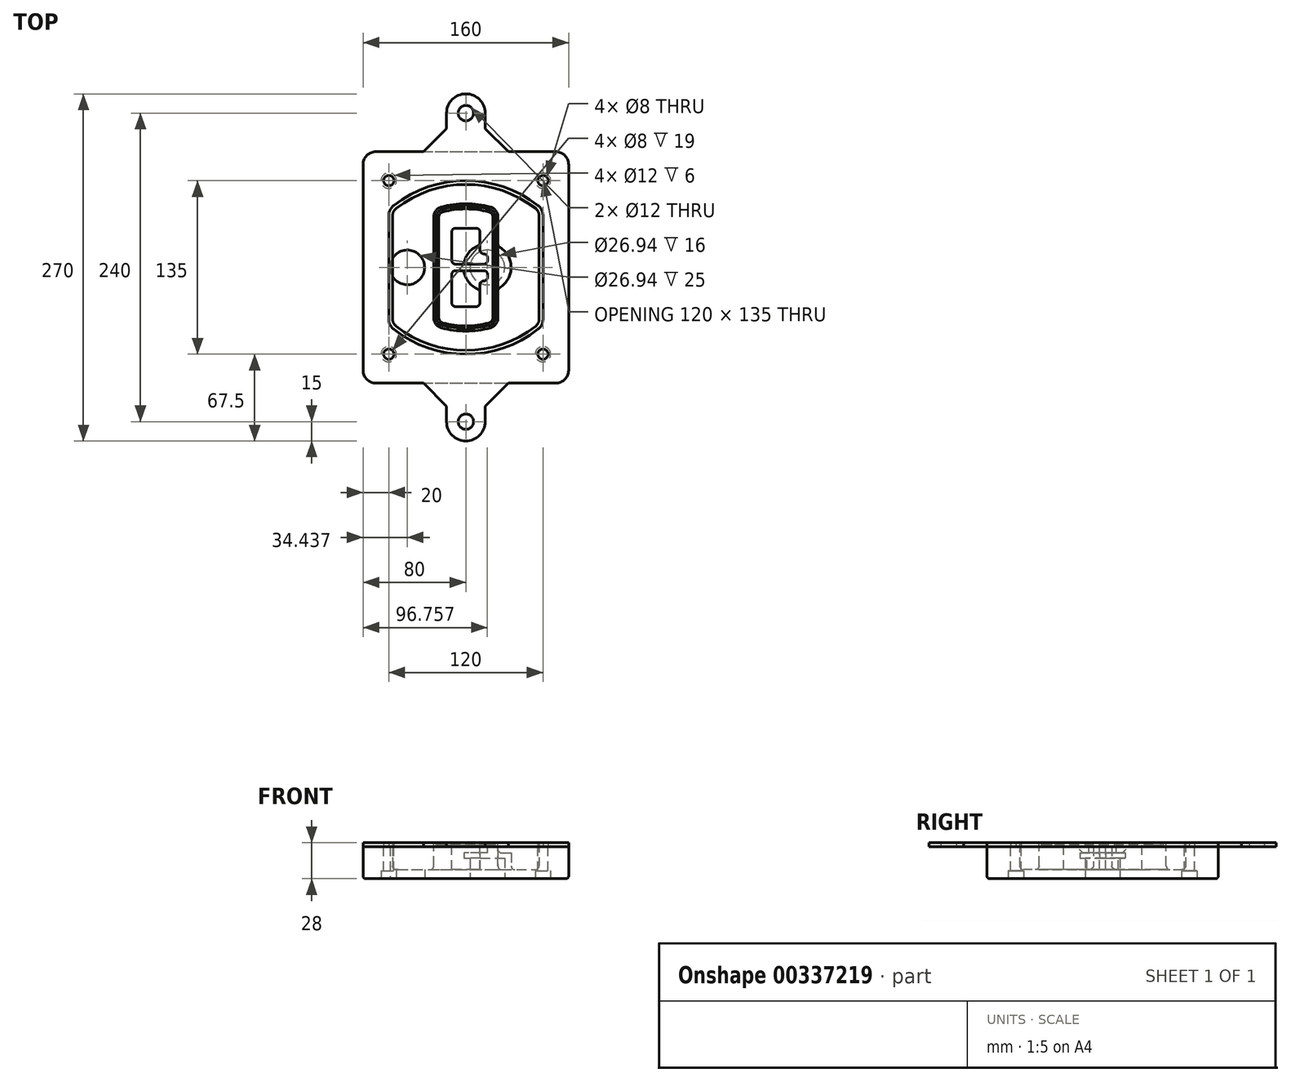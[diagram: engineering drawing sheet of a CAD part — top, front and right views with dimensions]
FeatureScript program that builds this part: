
annotation { "Feature Type Name" : "Feature", "Feature Type Description" : "" }
export const myFeature = defineFeature(function(context is Context, id is Id, definition is map)
    precondition{}
    {
        {
            var Q0;
            Q0=qCreatedBy(makeId("Top.planeOp"),FACE);
            var sketch = newSketch(context, id + "F0", { "sketchPlane" : qUnion([Q0])});
            skPoint(sketch, "E0.rect.middle", {"position": v(0, 0) * mm});
            skLineSegment(sketch, "E1.bottom", {"start": v(-70, -90) * mm, "end": v(70, -90) * mm});
            skLineSegment(sketch, "E1.top", {"start": v(-70, 90) * mm, "end": v(70, 90) * mm});
            skLineSegment(sketch, "E1.left", {"start": v(-80, -80) * mm, "end": v(-80, 80) * mm});
            skLineSegment(sketch, "E1.right", {"start": v(80, -80) * mm, "end": v(80, 80) * mm});
            skLineSegment(sketch, "E2", {"start": v(-80, 90) * mm, "end": v(80, -90) * mm, "construction": true});
            skLineSegment(sketch, "E3", {"start": v(80, 90) * mm, "end": v(-80, -90) * mm, "construction": true});
            skCircle(sketch, "E4", {"center": v(-60, 67.5) * mm, "radius": 4 * mm});
            skCircle(sketch, "E5", {"center": v(60, 67.5) * mm, "radius": 4 * mm});
            skCircle(sketch, "E6", {"center": v(60, -67.5) * mm, "radius": 4 * mm});
            skCircle(sketch, "E7", {"center": v(-60, -67.5) * mm, "radius": 4 * mm});
            skLineSegment(sketch, "E8", {"start": v(-60, 67.5) * mm, "end": v(60, 67.5) * mm, "construction": true});
            skLineSegment(sketch, "E9", {"start": v(60, 67.5) * mm, "end": v(60, -67.5) * mm, "construction": true});
            skLineSegment(sketch, "E10", {"start": v(60, -67.5) * mm, "end": v(-60, -67.5) * mm, "construction": true});
            skLineSegment(sketch, "E11", {"start": v(-60, -67.5) * mm, "end": v(-60, 67.5) * mm, "construction": true});
            skLineSegment(sketch, "E12", {"start": v(-60, 40.3) * mm, "end": v(-60, -40.3) * mm});
            skLineSegment(sketch, "E13", {"start": v(60, 40.3) * mm, "end": v(60, -40.3) * mm});
            skArc(sketch, "E14", {"start": v(56.15, 48.18) * mm, "mid": v(0, 67.5) * mm, "end": v(-56.15, 48.18) * mm});
            skArc(sketch, "E15", {"start": v(-56.15, -48.18) * mm, "mid": v(0, -67.5) * mm, "end": v(56.15, -48.18) * mm});
            skLineSegment(sketch, "E16", {"start": v(-60, 0) * mm, "end": v(60, 0) * mm, "construction": true});
            skPoint(sketch, "E17.visualSharp", {"position": v(-60, -45) * mm});
            skArc(sketch, "E17.filletArc", {"start": v(-60, -40.3) * mm, "mid": v(-58.99, -44.68) * mm, "end": v(-56.15, -48.18) * mm});
            skPoint(sketch, "E18.visualSharp", {"position": v(-60, 45) * mm});
            skArc(sketch, "E18.filletArc", {"start": v(-56.15, 48.18) * mm, "mid": v(-58.99, 44.68) * mm, "end": v(-60, 40.3) * mm});
            skPoint(sketch, "E19.visualSharp", {"position": v(60, 45) * mm});
            skArc(sketch, "E19.filletArc", {"start": v(60, 40.3) * mm, "mid": v(58.99, 44.68) * mm, "end": v(56.15, 48.18) * mm});
            skPoint(sketch, "E20.visualSharp", {"position": v(60, -45) * mm});
            skArc(sketch, "E20.filletArc", {"start": v(56.15, -48.18) * mm, "mid": v(58.99, -44.68) * mm, "end": v(60, -40.3) * mm});
            skPoint(sketch, "E21.visualSharp", {"position": v(-80, 90) * mm});
            skArc(sketch, "E21.filletArc", {"start": v(-70, 90) * mm, "mid": v(-77.07, 87.07) * mm, "end": v(-80, 80) * mm});
            skPoint(sketch, "E22.visualSharp", {"position": v(80, 90) * mm});
            skArc(sketch, "E22.filletArc", {"start": v(80, 80) * mm, "mid": v(77.07, 87.07) * mm, "end": v(70, 90) * mm});
            skPoint(sketch, "E23.visualSharp", {"position": v(80, -90) * mm});
            skArc(sketch, "E23.filletArc", {"start": v(70, -90) * mm, "mid": v(77.07, -87.07) * mm, "end": v(80, -80) * mm});
            skPoint(sketch, "E24.visualSharp", {"position": v(-80, -90) * mm});
            skArc(sketch, "E24.filletArc", {"start": v(-80, -80) * mm, "mid": v(-77.07, -87.07) * mm, "end": v(-70, -90) * mm});
            skArc(sketch, "E25.0", {"start": v(57, 40.3) * mm, "mid": v(56.3, 43.36) * mm, "end": v(54.3, 45.81) * mm});
            skLineSegment(sketch, "E25.1", {"start": v(57, 40.3) * mm, "end": v(57, -40.3) * mm});
            skArc(sketch, "E25.2", {"start": v(54.3, -45.81) * mm, "mid": v(56.3, -43.36) * mm, "end": v(57, -40.3) * mm});
            skArc(sketch, "E25.3", {"start": v(-54.3, -45.81) * mm, "mid": v(0, -64.5) * mm, "end": v(54.3, -45.81) * mm});
            skArc(sketch, "E25.4", {"start": v(-57, -40.3) * mm, "mid": v(-56.3, -43.36) * mm, "end": v(-54.3, -45.81) * mm});
            skArc(sketch, "E25.5", {"start": v(54.3, 45.81) * mm, "mid": v(0, 64.5) * mm, "end": v(-54.3, 45.81) * mm});
            skLineSegment(sketch, "E25.6", {"start": v(-57, 40.3) * mm, "end": v(-57, -40.3) * mm});
            skArc(sketch, "E25.7", {"start": v(-54.3, 45.81) * mm, "mid": v(-56.3, 43.36) * mm, "end": v(-57, 40.3) * mm});
            skArc(sketch, "E26.0", {"start": v(-58.62, 51.33) * mm, "mid": v(-62.58, 46.43) * mm, "end": v(-64, 40.3) * mm});
            skArc(sketch, "E26.1", {"start": v(58.62, 51.33) * mm, "mid": v(0, 71.5) * mm, "end": v(-58.62, 51.33) * mm});
            skArc(sketch, "E26.2", {"start": v(64, 40.3) * mm, "mid": v(62.58, 46.43) * mm, "end": v(58.62, 51.33) * mm});
            skLineSegment(sketch, "E26.3", {"start": v(64, 40.3) * mm, "end": v(64, -40.3) * mm});
            skArc(sketch, "E26.4", {"start": v(58.62, -51.33) * mm, "mid": v(62.58, -46.43) * mm, "end": v(64, -40.3) * mm});
            skLineSegment(sketch, "E26.5", {"start": v(-64, 40.3) * mm, "end": v(-64, -40.3) * mm});
            skArc(sketch, "E26.6", {"start": v(-58.62, -51.33) * mm, "mid": v(0, -71.5) * mm, "end": v(58.62, -51.33) * mm});
            skArc(sketch, "E26.7", {"start": v(-64, -40.3) * mm, "mid": v(-62.58, -46.43) * mm, "end": v(-58.62, -51.33) * mm});
            skSolve(sketch);
        }
        {
            var Q0;
            Q0=makeQuery(id+"F0.imprint","IMPRINT",FACE,{"disambiguationData":[TD([[makeQuery(id+"F0.imprint","IMPRINT",EDGE,{"derivedFrom":sQuery(id+"F0.wireOp",EDGE,"E1.bottom")}),1.0]])]});
            var Q1;
            Q1=makeQuery(id+"F0.imprint","IMPRINT",FACE,{"disambiguationData":[TD([[makeQuery(id+"F0.imprint","IMPRINT",EDGE,{"derivedFrom":sQuery(id+"F0.wireOp",EDGE,"E12")}),1.0]])]});
            var Q2;
            Q2=makeQuery(id+"F0.imprint","IMPRINT",FACE,{"disambiguationData":[TD([[makeQuery(id+"F0.imprint","IMPRINT",EDGE,{"derivedFrom":sQuery(id+"F0.wireOp",EDGE,"E25.0")}),1.0]])]});
            var Q3;
            Q3=makeQuery(id+"F0.imprint","IMPRINT",FACE,{"disambiguationData":[TD([[makeQuery(id+"F0.imprint","IMPRINT",EDGE,{"derivedFrom":sQuery(id+"F0.wireOp",EDGE,"E12")}),-1.0]])]});
            extrude(context, id + "F1", {"entities" : qUnion([Q0, Q1, Q2, Q3]), "oppositeDirection" : true, "depth" : 25 * mm});
        }
        {
            var Q0;
            Q0=makeQuery(id+"F0.imprint","IMPRINT",FACE,{"disambiguationData":[TD([[makeQuery(id+"F0.imprint","IMPRINT",EDGE,{"derivedFrom":sQuery(id+"F0.wireOp",EDGE,"E12")}),1.0]])]});
            extrude(context, id + "F2", {"entities" : qUnion([Q0]), "operationType" : NewBodyOperationType.ADD, "depth" : 3 * mm});
        }
        {
            var Q0;
            Q0=makeQuery(id+"F0.imprint","IMPRINT",FACE,{"disambiguationData":[TD([[makeQuery(id+"F0.imprint","IMPRINT",EDGE,{"derivedFrom":sQuery(id+"F0.wireOp",EDGE,"E25.0")}),1.0]])]});
            extrude(context, id + "F3", {"entities" : qUnion([Q0]), "operationType" : NewBodyOperationType.REMOVE, "oppositeDirection" : true, "depth" : 18 * mm});
        }
        {
            var Q0;
            Q0=makeQuery(id+"F2.opExtrude","CAP_FACE",FACE,{"disambiguationData":[OSD([sQuery(id+"F0.wireOp",EDGE,"E12"),sQuery(id+"F0.wireOp",EDGE,"E13"),sQuery(id+"F0.wireOp",EDGE,"E14"),sQuery(id+"F0.wireOp",EDGE,"E15"),sQuery(id+"F0.wireOp",EDGE,"E17.filletArc"),sQuery(id+"F0.wireOp",EDGE,"E18.filletArc"),sQuery(id+"F0.wireOp",EDGE,"E19.filletArc"),sQuery(id+"F0.wireOp",EDGE,"E20.filletArc"),sQuery(id+"F0.wireOp",EDGE,"E25.0"),sQuery(id+"F0.wireOp",EDGE,"E25.1"),sQuery(id+"F0.wireOp",EDGE,"E25.2"),sQuery(id+"F0.wireOp",EDGE,"E25.3"),sQuery(id+"F0.wireOp",EDGE,"E25.4"),sQuery(id+"F0.wireOp",EDGE,"E25.5"),sQuery(id+"F0.wireOp",EDGE,"E25.6"),sQuery(id+"F0.wireOp",EDGE,"E25.7")])],"isStart":false});
            var sketch = newSketch(context, id + "F4", { "sketchPlane" : qUnion([Q0])});
            skArc(sketch, "E27.0", {"start": v(-19.08, -46.97) * mm, "mid": v(0, -49.5) * mm, "end": v(19.08, -46.97) * mm});
            skArc(sketch, "E28.0", {"start": v(19.08, 46.97) * mm, "mid": v(0, 49.5) * mm, "end": v(-19.08, 46.97) * mm});
            skLineSegment(sketch, "E29", {"start": v(-25, 39.25) * mm, "end": v(-25, -39.25) * mm});
            skLineSegment(sketch, "E30", {"start": v(25, 39.25) * mm, "end": v(25, -39.25) * mm});
            skLineSegment(sketch, "E31", {"start": v(-25, 45.1) * mm, "end": v(25, 45.1) * mm, "construction": true});
            skLineSegment(sketch, "E32", {"start": v(-25, -45.1) * mm, "end": v(25, -45.1) * mm, "construction": true});
            skPoint(sketch, "E33.visualSharp", {"position": v(-25, 45.1) * mm});
            skArc(sketch, "E33.filletArc", {"start": v(-19.08, 46.97) * mm, "mid": v(-23.35, 44.11) * mm, "end": v(-25, 39.25) * mm});
            skPoint(sketch, "E34.visualSharp", {"position": v(25, 45.1) * mm});
            skArc(sketch, "E34.filletArc", {"start": v(25, 39.25) * mm, "mid": v(23.35, 44.11) * mm, "end": v(19.08, 46.97) * mm});
            skPoint(sketch, "E35.visualSharp", {"position": v(25, -45.1) * mm});
            skArc(sketch, "E35.filletArc", {"start": v(19.08, -46.97) * mm, "mid": v(23.35, -44.11) * mm, "end": v(25, -39.25) * mm});
            skPoint(sketch, "E36.visualSharp", {"position": v(-25, -45.1) * mm});
            skArc(sketch, "E36.filletArc", {"start": v(-25, -39.25) * mm, "mid": v(-23.35, -44.11) * mm, "end": v(-19.08, -46.97) * mm});
            skArc(sketch, "E37.0", {"start": v(54.3, 45.81) * mm, "mid": v(0, 64.5) * mm, "end": v(-54.3, 45.81) * mm});
            skArc(sketch, "E37.1", {"start": v(-54.3, 45.81) * mm, "mid": v(-56.3, 43.36) * mm, "end": v(-57, 40.3) * mm});
            skLineSegment(sketch, "E37.2", {"start": v(-57, 40.3) * mm, "end": v(-57, -40.3) * mm});
            skArc(sketch, "E37.3", {"start": v(-57, -40.3) * mm, "mid": v(-56.3, -43.36) * mm, "end": v(-54.3, -45.81) * mm});
            skArc(sketch, "E37.4", {"start": v(-54.3, -45.81) * mm, "mid": v(0, -64.5) * mm, "end": v(54.3, -45.81) * mm});
            skArc(sketch, "E37.5", {"start": v(54.3, -45.81) * mm, "mid": v(56.3, -43.36) * mm, "end": v(57, -40.3) * mm});
            skLineSegment(sketch, "E37.6", {"start": v(57, 40.3) * mm, "end": v(57, -40.3) * mm});
            skArc(sketch, "E37.7", {"start": v(57, 40.3) * mm, "mid": v(56.3, 43.36) * mm, "end": v(54.3, 45.81) * mm});
            skLineSegment(sketch, "E38.0", {"start": v(23, 39.25) * mm, "end": v(23, -39.25) * mm});
            skArc(sketch, "E38.1", {"start": v(18.56, -45.04) * mm, "mid": v(21.76, -42.9) * mm, "end": v(23, -39.25) * mm});
            skArc(sketch, "E38.2", {"start": v(-18.56, -45.04) * mm, "mid": v(0, -47.5) * mm, "end": v(18.56, -45.04) * mm});
            skArc(sketch, "E38.3", {"start": v(-23, -39.25) * mm, "mid": v(-21.76, -42.9) * mm, "end": v(-18.56, -45.04) * mm});
            skLineSegment(sketch, "E38.4", {"start": v(-23, 39.25) * mm, "end": v(-23, -39.25) * mm});
            skArc(sketch, "E38.5", {"start": v(23, 39.25) * mm, "mid": v(21.76, 42.9) * mm, "end": v(18.56, 45.04) * mm});
            skArc(sketch, "E38.6", {"start": v(-18.56, 45.04) * mm, "mid": v(-21.76, 42.9) * mm, "end": v(-23, 39.25) * mm});
            skArc(sketch, "E38.7", {"start": v(18.56, 45.04) * mm, "mid": v(0, 47.5) * mm, "end": v(-18.56, 45.04) * mm});
            skArc(sketch, "E39.0", {"start": v(21, 39.25) * mm, "mid": v(20.18, 41.68) * mm, "end": v(18.04, 43.1) * mm});
            skLineSegment(sketch, "E39.1", {"start": v(21, 39.25) * mm, "end": v(21, -39.25) * mm});
            skArc(sketch, "E39.2", {"start": v(18.04, -43.1) * mm, "mid": v(20.18, -41.68) * mm, "end": v(21, -39.25) * mm});
            skArc(sketch, "E39.3", {"start": v(-18.04, -43.1) * mm, "mid": v(0, -45.5) * mm, "end": v(18.04, -43.1) * mm});
            skArc(sketch, "E39.4", {"start": v(-21, -39.25) * mm, "mid": v(-20.18, -41.68) * mm, "end": v(-18.04, -43.1) * mm});
            skArc(sketch, "E39.5", {"start": v(18.04, 43.1) * mm, "mid": v(0, 45.5) * mm, "end": v(-18.04, 43.1) * mm});
            skLineSegment(sketch, "E39.6", {"start": v(-21, 39.25) * mm, "end": v(-21, -39.25) * mm});
            skArc(sketch, "E39.7", {"start": v(-18.04, 43.1) * mm, "mid": v(-20.18, 41.68) * mm, "end": v(-21, 39.25) * mm});
            skLineSegment(sketch, "E40", {"start": v(-25, 0) * mm, "end": v(25, 0) * mm, "construction": true});
            skLineSegment(sketch, "E41", {"start": v(-11, 5.5) * mm, "end": v(-11, 27.5) * mm});
            skLineSegment(sketch, "E42", {"start": v(-8, 30.5) * mm, "end": v(8, 30.5) * mm});
            skLineSegment(sketch, "E43", {"start": v(11, 27.5) * mm, "end": v(11, 13.5) * mm});
            skLineSegment(sketch, "E44", {"start": v(14, 10.5) * mm, "end": v(14, 10.5) * mm});
            skLineSegment(sketch, "E45", {"start": v(17, 7.5) * mm, "end": v(17, 5.5) * mm});
            skLineSegment(sketch, "E46", {"start": v(14, 2.5) * mm, "end": v(-8, 2.5) * mm});
            skPoint(sketch, "E47.visualSharp", {"position": v(-11, 30.5) * mm});
            skArc(sketch, "E47.filletArc", {"start": v(-8, 30.5) * mm, "mid": v(-10.12, 29.62) * mm, "end": v(-11, 27.5) * mm});
            skPoint(sketch, "E48.visualSharp", {"position": v(11, 30.5) * mm});
            skArc(sketch, "E48.filletArc", {"start": v(11, 27.5) * mm, "mid": v(10.12, 29.62) * mm, "end": v(8, 30.5) * mm});
            skPoint(sketch, "E49.visualSharp", {"position": v(11, 10.5) * mm});
            skArc(sketch, "E49.filletArc", {"start": v(11, 13.5) * mm, "mid": v(11.88, 11.38) * mm, "end": v(14, 10.5) * mm});
            skPoint(sketch, "E50.visualSharp", {"position": v(17, 10.5) * mm});
            skArc(sketch, "E50.filletArc", {"start": v(17, 7.5) * mm, "mid": v(16.12, 9.62) * mm, "end": v(14, 10.5) * mm});
            skPoint(sketch, "E51.visualSharp", {"position": v(17, 2.5) * mm});
            skArc(sketch, "E51.filletArc", {"start": v(14, 2.5) * mm, "mid": v(16.12, 3.38) * mm, "end": v(17, 5.5) * mm});
            skPoint(sketch, "E52.visualSharp", {"position": v(-11, 2.5) * mm});
            skArc(sketch, "E52.filletArc", {"start": v(-11, 5.5) * mm, "mid": v(-10.12, 3.38) * mm, "end": v(-8, 2.5) * mm});
            skLineSegment(sketch, "E53.0.MirrorCS", {"start": v(14, -2.5) * mm, "end": v(-8, -2.5) * mm});
            skArc(sketch, "E54.0.MirrorCS", {"start": v(-11, -5.5) * mm, "mid": v(-10.12, -3.38) * mm, "end": v(-8, -2.5) * mm});
            skLineSegment(sketch, "E55.0.MirrorCS", {"start": v(-11, -5.5) * mm, "end": v(-11, -27.5) * mm});
            skArc(sketch, "E56.0.MirrorCS", {"start": v(-8, -30.5) * mm, "mid": v(-10.12, -29.62) * mm, "end": v(-11, -27.5) * mm});
            skLineSegment(sketch, "E57.0.MirrorCS", {"start": v(-8, -30.5) * mm, "end": v(8, -30.5) * mm});
            skArc(sketch, "E58.0.MirrorCS", {"start": v(11, -27.5) * mm, "mid": v(10.12, -29.62) * mm, "end": v(8, -30.5) * mm});
            skLineSegment(sketch, "E59.0.MirrorCS", {"start": v(11, -27.5) * mm, "end": v(11, -13.5) * mm});
            skArc(sketch, "E60.0.MirrorCS", {"start": v(11, -13.5) * mm, "mid": v(11.88, -11.38) * mm, "end": v(14, -10.5) * mm});
            skArc(sketch, "E61.0.MirrorCS", {"start": v(17, -7.5) * mm, "mid": v(16.12, -9.62) * mm, "end": v(14, -10.5) * mm});
            skLineSegment(sketch, "E62.0.MirrorCS", {"start": v(17, -7.5) * mm, "end": v(17, -5.5) * mm});
            skArc(sketch, "E63.0.MirrorCS", {"start": v(14, -2.5) * mm, "mid": v(16.12, -3.38) * mm, "end": v(17, -5.5) * mm});
            skSolve(sketch);
        }
        {
            var Q0;
            Q0=makeQuery(id+"F4.imprint","IMPRINT",FACE,{"disambiguationData":[TD([[makeQuery(id+"F4.imprint","IMPRINT",EDGE,{"derivedFrom":sQuery(id+"F4.wireOp",EDGE,"E27.0")}),1.0]])]});
            var Q1;
            Q1=makeQuery(id+"F4.imprint","IMPRINT",FACE,{"disambiguationData":[TD([[makeQuery(id+"F4.imprint","IMPRINT",EDGE,{"derivedFrom":sQuery(id+"F4.wireOp",EDGE,"E38.0")}),-1.0]])]});
            var Q2;
            Q2=makeQuery(id+"F4.imprint","IMPRINT",FACE,{"disambiguationData":[TD([[makeQuery(id+"F4.imprint","IMPRINT",EDGE,{"derivedFrom":sQuery(id+"F4.wireOp",EDGE,"E39.0")}),1.0]])]});
            extrude(context, id + "F5", {"entities" : qUnion([Q0, Q1, Q2]), "operationType" : NewBodyOperationType.ADD, "endBound" : BoundingType.UP_TO_NEXT, "oppositeDirection" : true, "depth" : 25 * mm});
        }
        {
            var Q0;
            Q0=makeQuery(id+"F4.imprint","IMPRINT",FACE,{"disambiguationData":[TD([[makeQuery(id+"F4.imprint","IMPRINT",EDGE,{"derivedFrom":sQuery(id+"F4.wireOp",EDGE,"E38.0")}),-1.0]])]});
            extrude(context, id + "F6", {"entities" : qUnion([Q0]), "operationType" : NewBodyOperationType.REMOVE, "oppositeDirection" : true, "depth" : 2 * mm});
        }
        {
            var Q0;
            Q0=makeQuery(id+"F1.opExtrude","CAP_FACE",FACE,{"disambiguationData":[OSD([sQuery(id+"F0.wireOp",EDGE,"E1.bottom"),sQuery(id+"F0.wireOp",EDGE,"E1.top"),sQuery(id+"F0.wireOp",EDGE,"E1.left"),sQuery(id+"F0.wireOp",EDGE,"E1.right"),sQuery(id+"F0.wireOp",EDGE,"E4"),sQuery(id+"F0.wireOp",EDGE,"E5"),sQuery(id+"F0.wireOp",EDGE,"E6"),sQuery(id+"F0.wireOp",EDGE,"E7"),sQuery(id+"F0.wireOp",EDGE,"E21.filletArc"),sQuery(id+"F0.wireOp",EDGE,"E22.filletArc"),sQuery(id+"F0.wireOp",EDGE,"E23.filletArc"),sQuery(id+"F0.wireOp",EDGE,"E24.filletArc")])],"isStart":false});
            var sketch = newSketch(context, id + "F7", { "sketchPlane" : qUnion([Q0])});
            skCircle(sketch, "E64", {"center": v(16.76, 0) * mm, "radius": 13.47 * mm});
            skCircle(sketch, "E65", {"center": v(-45.56, 0) * mm, "radius": 13.47 * mm});
            skLineSegment(sketch, "E66", {"start": v(80, 0) * mm, "end": v(-80, 0) * mm});
            skCircle(sketch, "E67", {"center": v(16.76, 0) * mm, "radius": 18.47 * mm});
            skCircle(sketch, "E68", {"center": v(60, -67.5) * mm, "radius": 6 * mm});
            skCircle(sketch, "E69", {"center": v(-60, -67.5) * mm, "radius": 6 * mm});
            skCircle(sketch, "E70", {"center": v(-60, 67.5) * mm, "radius": 6 * mm});
            skCircle(sketch, "E71", {"center": v(60, 67.5) * mm, "radius": 6 * mm});
            skSolve(sketch);
        }
        {
            var Q0;
            {var subQ1=sQuery(id+"F7.wireOp",EDGE,"E66");var subQ4=sQuery(id+"F7.wireOp",EDGE,"E64");var subQ6=makeQuery(id+"F7.imprint","INTERSECT",VERTEX,{"disambiguationData":[OD(0.0)],"derivedFrom":[subQ4,subQ1]});Q0=makeQuery(id+"F7.imprint","IMPRINT",FACE,{"disambiguationData":[TD([[makeQuery(id+"F7.imprint","IMPRINT",EDGE,{"disambiguationData":[TD([[subQ6,-1.0]])],"derivedFrom":subQ4}),-1.0]])]});}
            var Q1;
            {var subQ0=sQuery(id+"F7.wireOp",EDGE,"E66");var subQ1=sQuery(id+"F7.wireOp",EDGE,"E64");var subQ3=makeQuery(id+"F7.imprint","INTERSECT",VERTEX,{"disambiguationData":[OD(0.0)],"derivedFrom":[subQ1,subQ0]});Q1=makeQuery(id+"F7.imprint","IMPRINT",FACE,{"disambiguationData":[TD([[makeQuery(id+"F7.imprint","IMPRINT",EDGE,{"disambiguationData":[TD([[subQ3,-1.0]])],"derivedFrom":subQ1}),1.0]])]});}
            var Q2;
            {var subQ0=sQuery(id+"F7.wireOp",EDGE,"E66");var subQ1=sQuery(id+"F7.wireOp",EDGE,"E64");var subQ3=makeQuery(id+"F7.imprint","INTERSECT",VERTEX,{"disambiguationData":[OD(0.0)],"derivedFrom":[subQ1,subQ0]});Q2=makeQuery(id+"F7.imprint","IMPRINT",FACE,{"disambiguationData":[TD([[makeQuery(id+"F7.imprint","IMPRINT",EDGE,{"disambiguationData":[TD([[subQ3,1.0]])],"derivedFrom":subQ1}),1.0]])]});}
            var Q3;
            {var subQ1=sQuery(id+"F7.wireOp",EDGE,"E66");var subQ4=sQuery(id+"F7.wireOp",EDGE,"E64");var subQ6=makeQuery(id+"F7.imprint","INTERSECT",VERTEX,{"disambiguationData":[OD(0.0)],"derivedFrom":[subQ4,subQ1]});Q3=makeQuery(id+"F7.imprint","IMPRINT",FACE,{"disambiguationData":[TD([[makeQuery(id+"F7.imprint","IMPRINT",EDGE,{"disambiguationData":[TD([[subQ6,1.0]])],"derivedFrom":subQ4}),-1.0]])]});}
            extrude(context, id + "F8", {"entities" : qUnion([Q0, Q1, Q2, Q3]), "operationType" : NewBodyOperationType.ADD, "oppositeDirection" : true, "depth" : 20 * mm});
        }
        {
            var Q0;
            {var subQ0=sQuery(id+"F7.wireOp",EDGE,"E66");var subQ1=sQuery(id+"F7.wireOp",EDGE,"E64");var subQ3=makeQuery(id+"F7.imprint","INTERSECT",VERTEX,{"disambiguationData":[OD(0.0)],"derivedFrom":[subQ1,subQ0]});Q0=makeQuery(id+"F7.imprint","IMPRINT",FACE,{"disambiguationData":[TD([[makeQuery(id+"F7.imprint","IMPRINT",EDGE,{"disambiguationData":[TD([[subQ3,-1.0]])],"derivedFrom":subQ1}),1.0]])]});}
            var Q1;
            {var subQ0=sQuery(id+"F7.wireOp",EDGE,"E66");var subQ1=sQuery(id+"F7.wireOp",EDGE,"E64");var subQ3=makeQuery(id+"F7.imprint","INTERSECT",VERTEX,{"disambiguationData":[OD(0.0)],"derivedFrom":[subQ1,subQ0]});Q1=makeQuery(id+"F7.imprint","IMPRINT",FACE,{"disambiguationData":[TD([[makeQuery(id+"F7.imprint","IMPRINT",EDGE,{"disambiguationData":[TD([[subQ3,1.0]])],"derivedFrom":subQ1}),1.0]])]});}
            extrude(context, id + "F9", {"entities" : qUnion([Q0, Q1]), "operationType" : NewBodyOperationType.REMOVE, "oppositeDirection" : true, "depth" : 16 * mm});
        }
        {
            var Q0;
            {var subQ0=sQuery(id+"F7.wireOp",EDGE,"E66");var subQ1=sQuery(id+"F7.wireOp",EDGE,"E65");var subQ3=makeQuery(id+"F7.imprint","INTERSECT",VERTEX,{"disambiguationData":[OD(0.0)],"derivedFrom":[subQ1,subQ0]});Q0=makeQuery(id+"F7.imprint","IMPRINT",FACE,{"disambiguationData":[TD([[makeQuery(id+"F7.imprint","IMPRINT",EDGE,{"disambiguationData":[TD([[subQ3,-1.0]])],"derivedFrom":subQ1}),1.0]])]});}
            var Q1;
            {var subQ0=sQuery(id+"F7.wireOp",EDGE,"E66");var subQ1=sQuery(id+"F7.wireOp",EDGE,"E65");var subQ3=makeQuery(id+"F7.imprint","INTERSECT",VERTEX,{"disambiguationData":[OD(0.0)],"derivedFrom":[subQ1,subQ0]});Q1=makeQuery(id+"F7.imprint","IMPRINT",FACE,{"disambiguationData":[TD([[makeQuery(id+"F7.imprint","IMPRINT",EDGE,{"disambiguationData":[TD([[subQ3,1.0]])],"derivedFrom":subQ1}),1.0]])]});}
            extrude(context, id + "F10", {"entities" : qUnion([Q0, Q1]), "operationType" : NewBodyOperationType.REMOVE, "oppositeDirection" : true, "depth" : 25 * mm});
        }
        {
            var Q0;
            Q0=makeQuery(id+"F7.imprint","IMPRINT",FACE,{"disambiguationData":[TD([[makeQuery(id+"F7.imprint","IMPRINT",EDGE,{"derivedFrom":sQuery(id+"F7.wireOp",EDGE,"E68")}),1.0]])]});
            var Q1;
            Q1=makeQuery(id+"F7.imprint","IMPRINT",FACE,{"disambiguationData":[TD([[makeQuery(id+"F7.imprint","IMPRINT",EDGE,{"derivedFrom":makeQuery(id+"F1.opExtrude","CAP_EDGE",EDGE,{"disambiguationData":[OSD([sQuery(id+"F0.wireOp",EDGE,"E5")])],"isStart":false})}),-1.0]])]});
            var Q2;
            Q2=makeQuery(id+"F7.imprint","IMPRINT",FACE,{"disambiguationData":[TD([[makeQuery(id+"F7.imprint","IMPRINT",EDGE,{"derivedFrom":sQuery(id+"F7.wireOp",EDGE,"E69")}),1.0]])]});
            var Q3;
            Q3=makeQuery(id+"F7.imprint","IMPRINT",FACE,{"disambiguationData":[TD([[makeQuery(id+"F7.imprint","IMPRINT",EDGE,{"derivedFrom":makeQuery(id+"F1.opExtrude","CAP_EDGE",EDGE,{"disambiguationData":[OSD([sQuery(id+"F0.wireOp",EDGE,"E4")])],"isStart":false})}),-1.0]])]});
            var Q4;
            Q4=makeQuery(id+"F7.imprint","IMPRINT",FACE,{"disambiguationData":[TD([[makeQuery(id+"F7.imprint","IMPRINT",EDGE,{"derivedFrom":sQuery(id+"F7.wireOp",EDGE,"E70")}),1.0]])]});
            var Q5;
            Q5=makeQuery(id+"F7.imprint","IMPRINT",FACE,{"disambiguationData":[TD([[makeQuery(id+"F7.imprint","IMPRINT",EDGE,{"derivedFrom":makeQuery(id+"F1.opExtrude","CAP_EDGE",EDGE,{"disambiguationData":[OSD([sQuery(id+"F0.wireOp",EDGE,"E7")])],"isStart":false})}),-1.0]])]});
            var Q6;
            Q6=makeQuery(id+"F7.imprint","IMPRINT",FACE,{"disambiguationData":[TD([[makeQuery(id+"F7.imprint","IMPRINT",EDGE,{"derivedFrom":sQuery(id+"F7.wireOp",EDGE,"E71")}),1.0]])]});
            var Q7;
            Q7=makeQuery(id+"F7.imprint","IMPRINT",FACE,{"disambiguationData":[TD([[makeQuery(id+"F7.imprint","IMPRINT",EDGE,{"derivedFrom":makeQuery(id+"F1.opExtrude","CAP_EDGE",EDGE,{"disambiguationData":[OSD([sQuery(id+"F0.wireOp",EDGE,"E6")])],"isStart":false})}),-1.0]])]});
            extrude(context, id + "F11", {"entities" : qUnion([Q0, Q1, Q2, Q3, Q4, Q5, Q6, Q7]), "operationType" : NewBodyOperationType.REMOVE, "oppositeDirection" : true, "depth" : 6 * mm});
        }
        {
            var Q0;
            Q0=makeQuery(id+"F9.boolean.opBoolean","COPY",FACE,{"derivedFrom":makeQuery(id+"F9.opExtrude","CAP_FACE",FACE,{"disambiguationData":[OSD([sQuery(id+"F7.wireOp",EDGE,"E64")])],"isStart":false})});
            var sketch = newSketch(context, id + "F12", { "sketchPlane" : qUnion([Q0])});
            skArc(sketch, "E72.0", {"start": v(11, 17.55) * mm, "mid": v(2.57, 11.82) * mm, "end": v(-1.54, 2.5) * mm});
            skArc(sketch, "E72.1", {"start": v(-1.54, -2.5) * mm, "mid": v(2.57, -11.82) * mm, "end": v(11, -17.55) * mm});
            skLineSegment(sketch, "E73", {"start": v(-1.54, -2.5) * mm, "end": v(14, -2.5) * mm});
            skLineSegment(sketch, "E74.0", {"start": v(14, 2.5) * mm, "end": v(-1.54, 2.5) * mm});
            skArc(sketch, "E74.1", {"start": v(14, 2.5) * mm, "mid": v(16.12, 3.38) * mm, "end": v(17, 5.5) * mm});
            skLineSegment(sketch, "E74.2", {"start": v(17, 7.5) * mm, "end": v(17, 5.5) * mm});
            skArc(sketch, "E74.3", {"start": v(17, 7.5) * mm, "mid": v(16.12, 9.62) * mm, "end": v(14, 10.5) * mm});
            skArc(sketch, "E74.4", {"start": v(11, 13.5) * mm, "mid": v(11.88, 11.38) * mm, "end": v(14, 10.5) * mm});
            skLineSegment(sketch, "E74.5", {"start": v(11, 17.55) * mm, "end": v(11, 13.5) * mm});
            skLineSegment(sketch, "E74.7", {"start": v(14, -2.5) * mm, "end": v(-1.54, -2.5) * mm});
            skArc(sketch, "E74.8", {"start": v(14, -2.5) * mm, "mid": v(16.12, -3.38) * mm, "end": v(17, -5.5) * mm});
            skLineSegment(sketch, "E74.9", {"start": v(17, -7.5) * mm, "end": v(17, -5.5) * mm});
            skArc(sketch, "E74.10", {"start": v(17, -7.5) * mm, "mid": v(16.12, -9.62) * mm, "end": v(14, -10.5) * mm});
            skArc(sketch, "E74.11", {"start": v(11, -13.5) * mm, "mid": v(11.88, -11.38) * mm, "end": v(14, -10.5) * mm});
            skLineSegment(sketch, "E74.12", {"start": v(11, -17.55) * mm, "end": v(11, -13.5) * mm});
            skPoint(sketch, "E75.orphan", {"position": v(11, -27.5) * mm});
            skPoint(sketch, "E76.orphan", {"position": v(-8, -2.5) * mm});
            skPoint(sketch, "E77.orphan", {"position": v(-8, 2.5) * mm});
            skPoint(sketch, "E78.orphan", {"position": v(11, 27.5) * mm});
            skSolve(sketch);
        }
        {
            var Q0;
            {var subQ7=sQuery(id+"F12.wireOp",EDGE,"E72.0");var subQ14=sQuery(id+"F12.wireOp",EDGE,"E72.1");var subQ16=sQuery(id+"F12.wireOp",EDGE,"E74.1");var subQ18=sQuery(id+"F12.wireOp",EDGE,"E74.8");Q0=qUnion([makeQuery(id+"F12.imprint","IMPRINT",FACE,{"disambiguationData":[TD([[makeQuery(id+"F12.imprint","IMPRINT",EDGE,{"derivedFrom":subQ7}),1.0]])]}),makeQuery(id+"F12.imprint","IMPRINT",FACE,{"disambiguationData":[TD([[makeQuery(id+"F12.imprint","IMPRINT",EDGE,{"derivedFrom":subQ14}),1.0]])]}),makeQuery(id+"F12.imprint","IMPRINT",FACE,{"disambiguationData":[TD([[makeQuery(id+"F12.imprint","IMPRINT",EDGE,{"derivedFrom":subQ16}),1.0]])]}),makeQuery(id+"F12.imprint","IMPRINT",FACE,{"disambiguationData":[TD([[makeQuery(id+"F12.imprint","IMPRINT",EDGE,{"derivedFrom":subQ18}),-1.0]])]})]);}
            var Q1;
            Q1=makeQuery(id+"F5.boolean.opBoolean","SPLIT",FACE,{"disambiguationData":[TD([makeQuery(id+"F5.opExtrude","SWEPT_FACE",FACE,{"disambiguationData":[OSD([sQuery(id+"F4.wireOp",EDGE,"E41")])]})])],"derivedFrom":makeQuery(id+"F3.boolean.opBoolean","COPY",FACE,{"derivedFrom":makeQuery(id+"F3.opExtrude","CAP_FACE",FACE,{"disambiguationData":[OSD([sQuery(id+"F0.wireOp",EDGE,"E25.0"),sQuery(id+"F0.wireOp",EDGE,"E25.1"),sQuery(id+"F0.wireOp",EDGE,"E25.2"),sQuery(id+"F0.wireOp",EDGE,"E25.3"),sQuery(id+"F0.wireOp",EDGE,"E25.4"),sQuery(id+"F0.wireOp",EDGE,"E25.5"),sQuery(id+"F0.wireOp",EDGE,"E25.6"),sQuery(id+"F0.wireOp",EDGE,"E25.7")])],"isStart":false})})});
            extrude(context, id + "F13", {"entities" : qUnion([Q0]), "operationType" : NewBodyOperationType.REMOVE, "endBound" : BoundingType.UP_TO_SURFACE, "endBoundEntityFace" : qUnion([Q1]), "depth" : 25 * mm});
        }
        {
            var Q0;
            Q0=makeQuery(id+"F3.boolean.opBoolean","COPY",EDGE,{"derivedFrom":makeQuery(id+"F3.opExtrude","CAP_EDGE",EDGE,{"disambiguationData":[OSD([sQuery(id+"F0.wireOp",EDGE,"E25.6")])],"isStart":false})});
            var Q1;
            Q1=makeQuery(id+"F8.boolean.opBoolean","INTERSECT",EDGE,{"derivedFrom":[makeQuery(id+"F5.opExtrude","SWEPT_FACE",FACE,{"disambiguationData":[OSD([sQuery(id+"F4.wireOp",EDGE,"E30")])]}),makeQuery(id+"F8.opExtrude","CAP_FACE",FACE,{"disambiguationData":[OSD([sQuery(id+"F7.wireOp",EDGE,"E67")])],"isStart":false})]});
            var Q2;
            Q2=makeQuery(id+"F8.boolean.opBoolean","INTERSECT",EDGE,{"disambiguationData":[OD(1.0)],"derivedFrom":[makeQuery(id+"F5.opExtrude","SWEPT_FACE",FACE,{"disambiguationData":[OSD([sQuery(id+"F4.wireOp",EDGE,"E30")])]}),makeQuery(id+"F8.opExtrude","SWEPT_FACE",FACE,{"disambiguationData":[OSD([sQuery(id+"F7.wireOp",EDGE,"E67")])]})]});
            var Q3;
            {var subQ0=sQuery(id+"F4.wireOp",EDGE,"E30");Q3=makeQuery(id+"F8.boolean.opBoolean","SPLIT",EDGE,{"disambiguationData":[TD([makeQuery(id+"F5.opExtrude","SWEPT_FACE",FACE,{"disambiguationData":[OSD([sQuery(id+"F4.wireOp",EDGE,"E35.filletArc")])]})])],"derivedFrom":makeQuery(id+"F5.opExtrude","CAP_EDGE",EDGE,{"disambiguationData":[OSD([subQ0])],"isStart":false})});}
            var Q4;
            {var subQ0=sQuery(id+"F0.wireOp",EDGE,"E25.7");var subQ1=sQuery(id+"F0.wireOp",EDGE,"E25.1");var subQ2=sQuery(id+"F0.wireOp",EDGE,"E25.6");var subQ3=sQuery(id+"F0.wireOp",EDGE,"E25.5");var subQ4=sQuery(id+"F0.wireOp",EDGE,"E25.4");var subQ5=sQuery(id+"F0.wireOp",EDGE,"E25.0");var subQ6=sQuery(id+"F0.wireOp",EDGE,"E25.2");var subQ7=sQuery(id+"F0.wireOp",EDGE,"E25.3");Q4=makeQuery(id+"F8.boolean.opBoolean","INTERSECT",EDGE,{"derivedFrom":[makeQuery(id+"F5.boolean.opBoolean","SPLIT",FACE,{"disambiguationData":[TD([makeQuery(id+"F2.opExtrude","SWEPT_FACE",FACE,{"disambiguationData":[OSD([subQ5])]})])],"derivedFrom":makeQuery(id+"F3.boolean.opBoolean","COPY",FACE,{"derivedFrom":makeQuery(id+"F3.opExtrude","CAP_FACE",FACE,{"disambiguationData":[OSD([subQ5,subQ1,subQ6,subQ7,subQ4,subQ3,subQ2,subQ0])],"isStart":false})})}),makeQuery(id+"F8.opExtrude","SWEPT_FACE",FACE,{"disambiguationData":[OSD([sQuery(id+"F7.wireOp",EDGE,"E67")])]})]});}
            var Q5;
            Q5=makeQuery(id+"F8.boolean.opBoolean","INTERSECT",EDGE,{"disambiguationData":[OD(0.0)],"derivedFrom":[makeQuery(id+"F5.opExtrude","SWEPT_FACE",FACE,{"disambiguationData":[OSD([sQuery(id+"F4.wireOp",EDGE,"E30")])]}),makeQuery(id+"F8.opExtrude","SWEPT_FACE",FACE,{"disambiguationData":[OSD([sQuery(id+"F7.wireOp",EDGE,"E67")])]})]});
            fillet(context, id + "F14", {"entities" : qUnion([Q0, Q1, Q2, Q3, Q4, Q5]), "radius" : 3 * mm, "tangentPropagation" : true, "allowEdgeOverflow" : false});
        }
        {
            var Q0;
            Q0=makeQuery(id+"F1.opExtrude","CAP_EDGE",EDGE,{"disambiguationData":[OSD([sQuery(id+"F0.wireOp",EDGE,"E1.bottom")])],"isStart":false});
            fillet(context, id + "F15", {"entities" : qUnion([Q0]), "radius" : 2 * mm, "tangentPropagation" : true, "allowEdgeOverflow" : false});
        }
        {
            var Q0;
            {var subQ0=sQuery(id+"F0.wireOp",EDGE,"E21.filletArc");var subQ1=sQuery(id+"F0.wireOp",EDGE,"E7");var subQ2=sQuery(id+"F0.wireOp",EDGE,"E6");var subQ3=sQuery(id+"F0.wireOp",EDGE,"E5");var subQ4=sQuery(id+"F0.wireOp",EDGE,"E4");var subQ5=sQuery(id+"F0.wireOp",EDGE,"E22.filletArc");var subQ6=sQuery(id+"F0.wireOp",EDGE,"E1.bottom");var subQ7=sQuery(id+"F0.wireOp",EDGE,"E1.right");var subQ8=sQuery(id+"F0.wireOp",EDGE,"E1.top");var subQ9=sQuery(id+"F0.wireOp",EDGE,"E1.left");var subQ10=sQuery(id+"F0.wireOp",EDGE,"E23.filletArc");var subQ11=sQuery(id+"F0.wireOp",EDGE,"E24.filletArc");Q0=makeQuery(id+"F2.boolean.opBoolean","SPLIT",FACE,{"disambiguationData":[TD([makeQuery(id+"F1.opExtrude","SWEPT_FACE",FACE,{"disambiguationData":[OSD([subQ6])]})])],"derivedFrom":makeQuery(id+"F1.opExtrude","CAP_FACE",FACE,{"disambiguationData":[OSD([subQ6,subQ8,subQ9,subQ7,subQ4,subQ3,subQ2,subQ1,subQ0,subQ5,subQ10,subQ11])],"isStart":true})});}
            var sketch = newSketch(context, id + "F16", { "sketchPlane" : qUnion([Q0])});
            skLineSegment(sketch, "E79", {"start": v(0, 90) * mm, "end": v(0, 120) * mm, "construction": true});
            skCircle(sketch, "E80", {"center": v(0, 120) * mm, "radius": 6 * mm});
            skLineSegment(sketch, "E81", {"start": v(-15, 120) * mm, "end": v(-15, 108) * mm});
            skLineSegment(sketch, "E82", {"start": v(15, 120) * mm, "end": v(15, 108) * mm});
            skLineSegment(sketch, "E83", {"start": v(-15, 108) * mm, "end": v(-33, 90) * mm});
            skLineSegment(sketch, "E84", {"start": v(15, 108) * mm, "end": v(33, 90) * mm});
            skArc(sketch, "E85", {"start": v(15, 120) * mm, "mid": v(0, 135) * mm, "end": v(-15, 120) * mm});
            skLineSegment(sketch, "E86", {"start": v(80, 0) * mm, "end": v(-80, 0) * mm, "construction": true});
            skLineSegment(sketch, "E87.MirrorCS", {"start": v(-15, -108) * mm, "end": v(-33, -90) * mm});
            skLineSegment(sketch, "E88.MirrorCS", {"start": v(15, -108) * mm, "end": v(33, -90) * mm});
            skLineSegment(sketch, "E89.MirrorCS", {"start": v(15, -120) * mm, "end": v(15, -108) * mm});
            skLineSegment(sketch, "E90.MirrorCS", {"start": v(-15, -120) * mm, "end": v(-15, -108) * mm});
            skArc(sketch, "E91.MirrorCS", {"start": v(15, -120) * mm, "mid": v(0, -135) * mm, "end": v(-15, -120) * mm});
            skCircle(sketch, "E92.MirrorC", {"center": v(0, -120) * mm, "radius": 6 * mm});
            skLineSegment(sketch, "E93.MirrorCS", {"start": v(0, -90) * mm, "end": v(0, -120) * mm, "construction": true});
            skSolve(sketch);
        }
        {
            var Q0;
            Q0=makeQuery(id+"F16.imprint","IMPRINT",FACE,{"disambiguationData":[TD([[makeQuery(id+"F16.imprint","IMPRINT",EDGE,{"derivedFrom":makeQuery(id+"F1.opExtrude","CAP_EDGE",EDGE,{"disambiguationData":[OSD([sQuery(id+"F0.wireOp",EDGE,"E1.left")])],"isStart":true})}),-1.0]])]});
            var Q1;
            Q1=makeQuery(id+"F16.imprint","IMPRINT",FACE,{"disambiguationData":[TD([[makeQuery(id+"F16.imprint","IMPRINT",EDGE,{"derivedFrom":sQuery(id+"F16.wireOp",EDGE,"E80")}),-1.0]])]});
            var Q2;
            {var subQ1=sQuery(id+"F16.wireOp",EDGE,"E87.MirrorCS");Q2=makeQuery(id+"F16.imprint","IMPRINT",FACE,{"disambiguationData":[TD([[makeQuery(id+"F16.imprint","IMPRINT",EDGE,{"derivedFrom":subQ1}),-1.0]])]});}
            var Q3;
            Q3=makeQuery(id+"F2.opExtrude","CAP_FACE",FACE,{"disambiguationData":[OSD([sQuery(id+"F0.wireOp",EDGE,"E12"),sQuery(id+"F0.wireOp",EDGE,"E13"),sQuery(id+"F0.wireOp",EDGE,"E14"),sQuery(id+"F0.wireOp",EDGE,"E15"),sQuery(id+"F0.wireOp",EDGE,"E17.filletArc"),sQuery(id+"F0.wireOp",EDGE,"E18.filletArc"),sQuery(id+"F0.wireOp",EDGE,"E19.filletArc"),sQuery(id+"F0.wireOp",EDGE,"E20.filletArc"),sQuery(id+"F0.wireOp",EDGE,"E25.0"),sQuery(id+"F0.wireOp",EDGE,"E25.1"),sQuery(id+"F0.wireOp",EDGE,"E25.2"),sQuery(id+"F0.wireOp",EDGE,"E25.3"),sQuery(id+"F0.wireOp",EDGE,"E25.4"),sQuery(id+"F0.wireOp",EDGE,"E25.5"),sQuery(id+"F0.wireOp",EDGE,"E25.6"),sQuery(id+"F0.wireOp",EDGE,"E25.7")])],"isStart":false});
            extrude(context, id + "F17", {"entities" : qUnion([Q0, Q1, Q2]), "endBound" : BoundingType.UP_TO_SURFACE, "endBoundEntityFace" : qUnion([Q3]), "depth" : 25 * mm});
        }
    });
